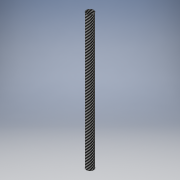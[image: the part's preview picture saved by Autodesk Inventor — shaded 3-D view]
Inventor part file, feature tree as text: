
AUTODESK INVENTOR PART (.ipt)
format: ipt  version: 2018 (Build 220112000, 112)  size: 109,056 bytes
history: native  units: in
note: dims shown in document units (in); Inventor stores cm internally (conversion verified against a paired STEP export)
features: extrude x1, sketch x1
ambient origin geometry x8: Origin, YZ Plane, XZ Plane, XY Plane, X Axis, Y Axis, Z Axis, Center Point
bodies: Solid1 (feature_tree)
feature tree (2):
  extrude  "Extrusion1"  Depth=7.8393in
  sketch  "Sketch1"  dims[d0=0.42in d1=0.39in d2=7.8393in d3=0.0in]
